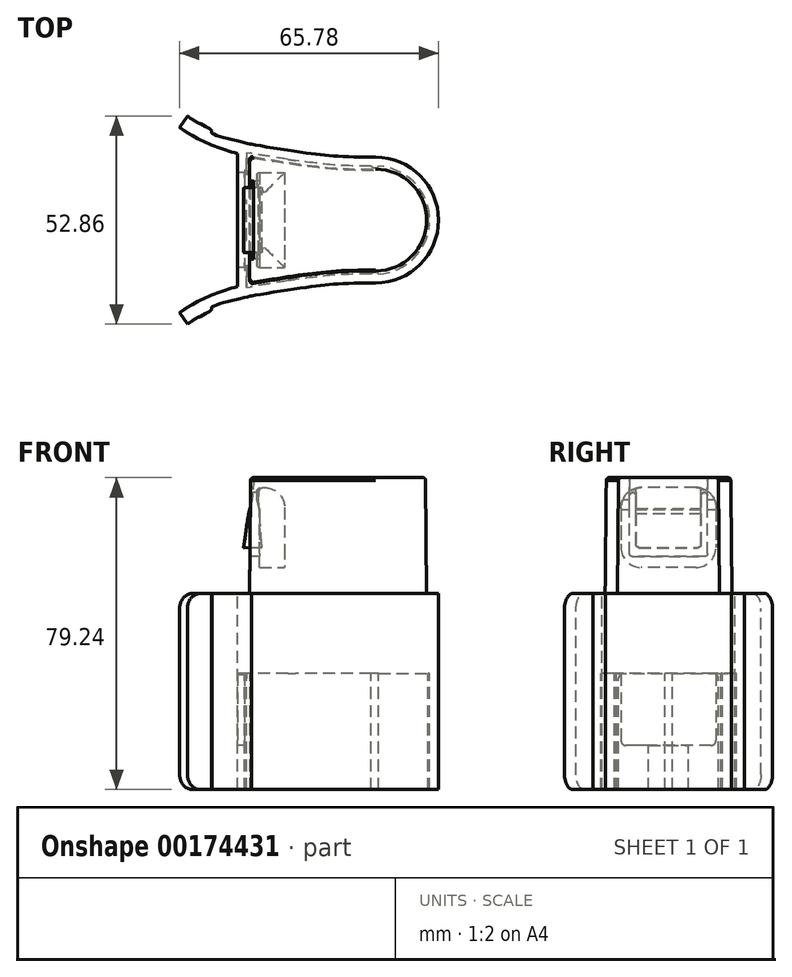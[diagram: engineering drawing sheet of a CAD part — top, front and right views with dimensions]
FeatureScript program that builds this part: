
annotation { "Feature Type Name" : "Feature", "Feature Type Description" : "" }
export const myFeature = defineFeature(function(context is Context, id is Id, definition is map)
    precondition{}
    {
        {
            var Q0;
            Q0=qCreatedBy(makeId("Top.planeOp"),FACE);
            var sketch = newSketch(context, id + "F0", { "sketchPlane" : qUnion([Q0])});
            skLineSegment(sketch, "E0", {"start": v(0, 0) * mm, "end": v(-39.58, 0) * mm, "construction": true});
            skArc(sketch, "E1", {"start": v(0, -12.95) * mm, "mid": v(12.95, 0) * mm, "end": v(0, 12.95) * mm});
            skLineSegment(sketch, "E2", {"start": v(-32, 16.26) * mm, "end": v(-32, -16.26) * mm});
            skPoint(sketch, "E3", {"position": v(-32, 0) * mm});
            skFitSpline(sketch, "E4", {"points": [v(0, 12.95) * mm, v(-14.22, 13.59) * mm, v(-32, 16.26) * mm], "startDerivative": vector(-40.46, 0) * mm, "endDerivative": vector(-35.46, 6.25) * mm});
            skLineSegment(sketch, "E5", {"start": v(-32, 16.26) * mm, "end": v(60.19, 0) * mm, "construction": true});
            skLineSegment(sketch, "E6", {"start": v(0, 12.95) * mm, "end": v(-13.28, 12.95) * mm, "construction": true});
            skFitSpline(sketch, "E7.MirrorCS", {"points": [v(0, -12.95) * mm, v(-14.22, -13.59) * mm, v(-32, -16.26) * mm], "startDerivative": vector(-40.46, 0) * mm, "endDerivative": vector(-35.46, -6.25) * mm});
            skSolve(sketch);
        }
        {
            var Q0;
            Q0=qCreatedBy(makeId("Top.planeOp"),FACE);
            var sketch = newSketch(context, id + "F1", { "sketchPlane" : qUnion([Q0])});
            skFitSpline(sketch, "E8.0", {"points": [v(0, 16) * mm, v(-1.67, 16) * mm, v(-4.6, 16.02) * mm, v(-7.54, 16.11) * mm, v(-9.71, 16.24) * mm, v(-11.32, 16.36) * mm, v(-12.96, 16.51) * mm, v(-14.7, 16.7) * mm, v(-16.57, 16.94) * mm, v(-19.19, 17.28) * mm, v(-22.67, 17.8) * mm, v(-27.05, 18.5) * mm, v(-30, 19) * mm, v(-31.47, 19.26) * mm]});
            skArc(sketch, "E8.1", {"start": v(0, -16) * mm, "mid": v(16, 0) * mm, "end": v(0, 16) * mm});
            skFitSpline(sketch, "E8.2", {"points": [v(0, -16) * mm, v(-1.67, -16) * mm, v(-4.6, -16.02) * mm, v(-7.54, -16.11) * mm, v(-9.71, -16.24) * mm, v(-11.32, -16.36) * mm, v(-12.96, -16.51) * mm, v(-14.7, -16.7) * mm, v(-16.57, -16.94) * mm, v(-19.19, -17.28) * mm, v(-22.67, -17.8) * mm, v(-27.05, -18.5) * mm, v(-30, -19) * mm, v(-31.47, -19.26) * mm]});
            skLineSegment(sketch, "E8.3", {"start": v(-35.05, 19.59) * mm, "end": v(-35.05, -19.59) * mm, "construction": true});
            skFitSpline(sketch, "E9", {"points": [v(-31.47, 19.26) * mm, v(-41.53, 22.07) * mm, v(-41.6, 22.64) * mm, v(-47.78, 26.43) * mm], "startDerivative": vector(1.67, -0.3) * mm, "endDerivative": vector(-19.6, 14.64) * mm});
            skArc(sketch, "E10", {"start": v(-49.78, 23.5) * mm, "mid": v(-41.28, 18.93) * mm, "end": v(-32, 16.26) * mm});
            skLineSegment(sketch, "E11", {"start": v(-47.78, 26.43) * mm, "end": v(-49.78, 23.5) * mm});
            skLineSegment(sketch, "E12", {"start": v(0, 0) * mm, "end": v(-91.75, 0) * mm, "construction": true});
            skLineSegment(sketch, "E13", {"start": v(-35.05, 16.9) * mm, "end": v(-35.05, -16.9) * mm});
            skPoint(sketch, "E14", {"position": v(-35.05, 0) * mm});
            skArc(sketch, "E15.MirrorCS", {"start": v(-49.78, -23.5) * mm, "mid": v(-41.28, -18.93) * mm, "end": v(-32, -16.26) * mm});
            skLineSegment(sketch, "E16.MirrorCS", {"start": v(-47.78, -26.43) * mm, "end": v(-49.78, -23.5) * mm});
            skFitSpline(sketch, "E17.MirrorCS", {"points": [v(-31.47, -19.26) * mm, v(-41.53, -22.07) * mm, v(-41.6, -22.64) * mm, v(-47.78, -26.43) * mm], "startDerivative": vector(1.67, 0.3) * mm, "endDerivative": vector(-19.6, -14.64) * mm});
            skSolve(sketch);
        }
        {
            var Q0;
            Q0=makeQuery(id+"F0.imprint","IMPRINT",FACE,{"disambiguationData":[TD([[makeQuery(id+"F0.imprint","IMPRINT",EDGE,{"derivedFrom":sQuery(id+"F0.wireOp",EDGE,"E1")}),1.0]])]});
            extrude(context, id + "F2", {"entities" : qUnion([Q0]), "depth" : 29.46 * mm, "hasDraft" : true, "draftAngle" : .5 * degree, "draftPullDirection" : true});
        }
        {
            var Q0;
            Q0 = qSketchRegion(id + "F1", true);
            extrude(context, id + "F3", {"entities" : qUnion([Q0]), "operationType" : NewBodyOperationType.ADD, "oppositeDirection" : true, "depth" : 49.78 * mm});
        }
        {
            var Q0;
            Q0=makeQuery(id+"F2.opExtrude","SWEPT_FACE",FACE,{"disambiguationData":[OSD([sQuery(id+"F0.wireOp",EDGE,"E2")])]});
            var sketch = newSketch(context, id + "F4", { "sketchPlane" : qUnion([Q0])});
            skLineSegment(sketch, "E18.bottom", {"start": v(-9.9, 25.38) * mm, "end": v(-8.26, 25.38) * mm});
            skLineSegment(sketch, "E18.top", {"start": v(-9.9, 9.12) * mm, "end": v(9.9, 9.12) * mm});
            skLineSegment(sketch, "E18.left", {"start": v(-9.9, 25.38) * mm, "end": v(-9.9, 9.12) * mm});
            skLineSegment(sketch, "E18.right", {"start": v(9.9, 25.38) * mm, "end": v(9.9, 9.12) * mm});
            skLineSegment(sketch, "E19.top", {"start": v(-8.26, 11.91) * mm, "end": v(8.26, 11.91) * mm});
            skLineSegment(sketch, "E19.left", {"start": v(-8.26, 25.38) * mm, "end": v(-8.26, 11.91) * mm});
            skLineSegment(sketch, "E19.right", {"start": v(8.26, 25.38) * mm, "end": v(8.26, 11.91) * mm});
            skLineSegment(sketch, "E20.trimOffspring", {"start": v(8.26, 25.38) * mm, "end": v(9.9, 25.38) * mm});
            skLineSegment(sketch, "E21", {"start": v(-8.26, 25.38) * mm, "end": v(8.26, 25.38) * mm, "construction": true});
            skPoint(sketch, "E22", {"position": v(0, 25.38) * mm});
            skPoint(sketch, "E23", {"position": v(0, 9.12) * mm});
            skSolve(sketch);
        }
        {
            var Q0;
            Q0=qCreatedBy(makeId("Top.planeOp"),FACE);
            cPlane(context, id + "F5", {"entities" : qUnion([Q0]), "cplaneType" : CPlaneType.OFFSET, "offset" : 20.32 * mm, "oppositeDirection" : true, "width" : 152.4 * mm, "height" : 152.4 * mm});
        }
        {
            var Q0;
            Q0=qCreatedBy(id+"F5.planeOp",FACE);
            var sketch = newSketch(context, id + "F6", { "sketchPlane" : qUnion([Q0])});
            skFitSpline(sketch, "E24.0", {"points": [v(0, 12.95) * mm, v(-6.35, 12.95) * mm, v(-13.52, 13.25) * mm, v(-25.75, 15.15) * mm, v(-32, 16.26) * mm], "construction": true});
            skArc(sketch, "E24.1", {"start": v(0, -12.95) * mm, "mid": v(12.95, 0) * mm, "end": v(0, 12.95) * mm, "construction": true});
            skFitSpline(sketch, "E24.2", {"points": [v(0, -12.95) * mm, v(-6.35, -12.95) * mm, v(-13.52, -13.25) * mm, v(-25.75, -15.15) * mm, v(-32, -16.26) * mm], "construction": true});
            skLineSegment(sketch, "E24.3", {"start": v(-32, 16.26) * mm, "end": v(-32, -16.26) * mm, "construction": true});
            skFitSpline(sketch, "E25.0", {"points": [v(0, 13.72) * mm, v(-1.68, 13.72) * mm, v(-4.63, 13.74) * mm, v(-7.63, 13.83) * mm, v(-9.86, 13.96) * mm, v(-11.51, 14.08) * mm, v(-13.19, 14.24) * mm, v(-14.96, 14.44) * mm, v(-16.86, 14.67) * mm, v(-19.5, 15.02) * mm, v(-23.02, 15.53) * mm, v(-27.42, 16.24) * mm, v(-30.4, 16.75) * mm, v(-31.87, 17) * mm]});
            skArc(sketch, "E25.1", {"start": v(0.77, -13.7) * mm, "mid": v(9.63, -9.76) * mm, "end": v(13.68, -0.95) * mm});
            skFitSpline(sketch, "E25.2", {"points": [v(0, -13.72) * mm, v(-1.68, -13.72) * mm, v(-4.63, -13.74) * mm, v(-7.63, -13.83) * mm, v(-9.86, -13.96) * mm, v(-11.51, -14.08) * mm, v(-13.19, -14.24) * mm, v(-14.96, -14.44) * mm, v(-16.86, -14.67) * mm, v(-19.5, -15.02) * mm, v(-23.02, -15.53) * mm, v(-27.42, -16.24) * mm, v(-30.4, -16.75) * mm, v(-31.87, -17) * mm]});
            skLineSegment(sketch, "E25.3", {"start": v(-32.77, 17.2) * mm, "end": v(-32.77, 12.7) * mm});
            skLineSegment(sketch, "E26", {"start": v(-31.87, 17) * mm, "end": v(-32.77, 17.2) * mm});
            skLineSegment(sketch, "E27", {"start": v(-31.87, -17) * mm, "end": v(-32.77, -17.17) * mm});
            skArc(sketch, "E28", {"start": v(13.68, 0.95) * mm, "mid": v(13.25, 0) * mm, "end": v(13.68, -0.95) * mm});
            skArc(sketch, "E29", {"start": v(-1.14, 13.72) * mm, "mid": v(-0.19, 13.28) * mm, "end": v(0.77, 13.7) * mm});
            skArc(sketch, "E30", {"start": v(-22.26, 15.43) * mm, "mid": v(-21.38, 14.86) * mm, "end": v(-20.38, 15.15) * mm});
            skArc(sketch, "E31", {"start": v(-20.38, -15.15) * mm, "mid": v(-21.38, -14.86) * mm, "end": v(-22.26, -15.43) * mm});
            skArc(sketch, "E32", {"start": v(0.77, -13.7) * mm, "mid": v(-0.19, -13.28) * mm, "end": v(-1.14, -13.72) * mm});
            skLineSegment(sketch, "E33.bottom", {"start": v(-32.77, -12.7) * mm, "end": v(-33.27, -12.7) * mm});
            skLineSegment(sketch, "E33.top", {"start": v(-32.77, -5.08) * mm, "end": v(-33.27, -5.08) * mm});
            skLineSegment(sketch, "E33.right", {"start": v(-33.27, -12.7) * mm, "end": v(-33.27, -5.08) * mm});
            skLineSegment(sketch, "E34.bottom", {"start": v(-32.77, 5.08) * mm, "end": v(-33.27, 5.08) * mm});
            skLineSegment(sketch, "E34.top", {"start": v(-32.77, 12.7) * mm, "end": v(-33.27, 12.7) * mm});
            skLineSegment(sketch, "E34.right", {"start": v(-33.27, 5.08) * mm, "end": v(-33.27, 12.7) * mm});
            skLineSegment(sketch, "E35", {"start": v(-33.27, -5.08) * mm, "end": v(-33.27, 5.08) * mm, "construction": true});
            skPoint(sketch, "E36", {"position": v(-33.27, 0) * mm});
            skLineSegment(sketch, "E37.trimOffspring", {"start": v(-32.77, -12.7) * mm, "end": v(-32.77, -17.17) * mm});
            skLineSegment(sketch, "E38.trimOffspring", {"start": v(-32.77, 5.08) * mm, "end": v(-32.77, -5.08) * mm});
            skFitSpline(sketch, "E39.trimOffspring", {"points": [v(0, -13.72) * mm, v(-1.68, -13.72) * mm, v(-4.63, -13.74) * mm, v(-7.63, -13.83) * mm, v(-9.86, -13.96) * mm, v(-11.51, -14.08) * mm, v(-13.19, -14.24) * mm, v(-14.96, -14.44) * mm, v(-16.86, -14.67) * mm, v(-19.5, -15.02) * mm, v(-23.02, -15.53) * mm, v(-27.42, -16.24) * mm, v(-30.4, -16.75) * mm, v(-31.87, -17) * mm]});
            skArc(sketch, "E40.trimOffspring", {"start": v(13.68, 0.95) * mm, "mid": v(9.63, 9.76) * mm, "end": v(0.77, 13.7) * mm});
            skFitSpline(sketch, "E41.trimOffspring", {"points": [v(0, 13.72) * mm, v(-1.68, 13.72) * mm, v(-4.63, 13.74) * mm, v(-7.63, 13.83) * mm, v(-9.86, 13.96) * mm, v(-11.51, 14.08) * mm, v(-13.19, 14.24) * mm, v(-14.96, 14.44) * mm, v(-16.86, 14.67) * mm, v(-19.5, 15.02) * mm, v(-23.02, 15.53) * mm, v(-27.42, 16.24) * mm, v(-30.4, 16.75) * mm, v(-31.87, 17) * mm]});
            skSolve(sketch);
        }
        {
            var Q0;
            Q0 = qSketchRegion(id + "F6", true);
            extrude(context, id + "F7", {"entities" : qUnion([Q0]), "operationType" : NewBodyOperationType.REMOVE, "endBound" : BoundingType.UP_TO_NEXT, "oppositeDirection" : true, "depth" : 25.4 * mm});
        }
        {
            var Q0;
            Q0=qCreatedBy(makeId("Front.planeOp"),FACE);
            var sketch = newSketch(context, id + "F8", { "sketchPlane" : qUnion([Q0])});
            skFitSpline(sketch, "E42.0.0", {"points": [v(-31.75, 29.46) * mm, v(-21.16, 29.46) * mm, v(-10.58, 29.46) * mm, v(0, 29.46) * mm], "construction": true});
            skLineSegment(sketch, "E42.0.1", {"start": v(0, 29.46) * mm, "end": v(12.7, 29.46) * mm, "construction": true});
            skFitSpline(sketch, "E42.0.2", {"points": [v(0, 29.46) * mm, v(-10.58, 29.46) * mm, v(-21.16, 29.46) * mm, v(-31.75, 29.46) * mm]});
            skFitSpline(sketch, "E43", {"points": [v(-31.06, 29.46) * mm, v(-31.3, 24.68) * mm, v(-32.59, 18.3) * mm, v(-33.38, 12.65) * mm, v(-33.5, 11.63) * mm], "startDerivative": vector(0.39, -18.89) * mm, "endDerivative": vector(0.18, -15.34) * mm});
            skLineSegment(sketch, "E44", {"start": v(-31.06, 29.46) * mm, "end": v(-33.94, 29.46) * mm});
            skLineSegment(sketch, "E45", {"start": v(-33.94, 29.46) * mm, "end": v(-33.5, 11.63) * mm});
            skLineSegment(sketch, "E46", {"start": v(-33.5, 11.63) * mm, "end": v(-28.87, 11.75) * mm});
            skLineSegment(sketch, "E47", {"start": v(-28.87, 11.75) * mm, "end": v(-29.77, 24.68) * mm});
            skArc(sketch, "E48", {"start": v(-27.53, 29.46) * mm, "mid": v(-29.27, 27.36) * mm, "end": v(-29.77, 24.68) * mm});
            skLineSegment(sketch, "E49", {"start": v(-31.06, 29.46) * mm, "end": v(-27.53, 29.46) * mm});
            skSolve(sketch);
        }
        {
            var Q0;
            {var subQ0=sQuery(id+"F8.wireOp",EDGE,"E43");Q0=makeQuery(id+"F8.imprint","IMPRINT",FACE,{"disambiguationData":[TD([[makeQuery(id+"F8.imprint","IMPRINT",EDGE,{"derivedFrom":subQ0}),-1.0]])]});}
            extrude(context, id + "F9", {"entities" : qUnion([Q0]), "operationType" : NewBodyOperationType.REMOVE, "endBound" : BoundingType.SYMMETRIC, "depth" : 19.8 * mm});
        }
        {
            var Q0;
            Q0=qCreatedBy(makeId("Front.planeOp"),FACE);
            var sketch = newSketch(context, id + "F10", { "sketchPlane" : qUnion([Q0])});
            skLineSegment(sketch, "E50.bottom", {"start": v(-29.46, 26.92) * mm, "end": v(-23.11, 26.92) * mm});
            skLineSegment(sketch, "E50.top", {"start": v(-29.46, 6.6) * mm, "end": v(-23.11, 6.6) * mm});
            skLineSegment(sketch, "E50.left", {"start": v(-29.46, 26.92) * mm, "end": v(-29.46, 6.6) * mm});
            skLineSegment(sketch, "E50.right", {"start": v(-23.11, 26.92) * mm, "end": v(-23.11, 6.6) * mm});
            skLineSegment(sketch, "E51", {"start": v(-29.46, 26.92) * mm, "end": v(-30.1, 26.28) * mm});
            skLineSegment(sketch, "E52", {"start": v(-30.1, 26.28) * mm, "end": v(-30.1, 23.83) * mm});
            skLineSegment(sketch, "E53", {"start": v(-30.1, 23.83) * mm, "end": v(-29.46, 21.25) * mm});
            skSolve(sketch);
        }
        {
            var Q0;
            Q0 = qSketchRegion(id + "F10", true);
            extrude(context, id + "F11", {"entities" : qUnion([Q0]), "operationType" : NewBodyOperationType.REMOVE, "endBound" : BoundingType.SYMMETRIC, "oppositeDirection" : true, "depth" : 24.13 * mm});
        }
        {
            var Q0;
            Q0 = qSketchRegion(id + "F4", true);
            extrude(context, id + "F12", {"entities" : qUnion([Q0]), "operationType" : NewBodyOperationType.REMOVE, "endBound" : BoundingType.UP_TO_NEXT, "oppositeDirection" : true, "depth" : 25.4 * mm});
        }
        {
            var Q0;
            Q0=makeQuery(id+"F8.imprint","IMPRINT",FACE,{"disambiguationData":[TD([[makeQuery(id+"F8.imprint","IMPRINT",EDGE,{"derivedFrom":sQuery(id+"F8.wireOp",EDGE,"E43")}),1.0]])]});
            extrude(context, id + "F13", {"entities" : qUnion([Q0]), "operationType" : NewBodyOperationType.ADD, "endBound" : BoundingType.SYMMETRIC, "depth" : 16.5 * mm});
        }
        {
            var Q0;
            Q0=makeQuery(id+"F13.opExtrude","CAP_EDGE",EDGE,{"disambiguationData":[OSD([sQuery(id+"F8.wireOp",EDGE,"E46")])],"isStart":true});
            var Q1;
            Q1=makeQuery(id+"F13.opExtrude","CAP_EDGE",EDGE,{"disambiguationData":[OSD([sQuery(id+"F8.wireOp",EDGE,"E46")])],"isStart":false});
            var Q2;
            Q2=makeQuery(id+"F12.boolean.opBoolean","COPY",EDGE,{"derivedFrom":makeQuery(id+"F12.opExtrude","SWEPT_EDGE",EDGE,{"disambiguationData":[OSD([sQuery(id+"F4.wireOp",EDGE,"E18.right"),sQuery(id+"F4.wireOp",EDGE,"E20.trimOffspring")])]})});
            var Q3;
            Q3=makeQuery(id+"F12.boolean.opBoolean","COPY",EDGE,{"derivedFrom":makeQuery(id+"F12.opExtrude","SWEPT_EDGE",EDGE,{"disambiguationData":[OSD([sQuery(id+"F4.wireOp",EDGE,"E19.right"),sQuery(id+"F4.wireOp",EDGE,"E20.trimOffspring")])]})});
            var Q4;
            Q4=makeQuery(id+"F12.boolean.opBoolean","COPY",EDGE,{"derivedFrom":makeQuery(id+"F12.opExtrude","SWEPT_EDGE",EDGE,{"disambiguationData":[OSD([sQuery(id+"F4.wireOp",EDGE,"E18.bottom"),sQuery(id+"F4.wireOp",EDGE,"E18.left")])]})});
            var Q5;
            Q5=makeQuery(id+"F12.boolean.opBoolean","COPY",EDGE,{"derivedFrom":makeQuery(id+"F12.opExtrude","SWEPT_EDGE",EDGE,{"disambiguationData":[OSD([sQuery(id+"F4.wireOp",EDGE,"E18.top"),sQuery(id+"F4.wireOp",EDGE,"E18.left")])]})});
            var Q6;
            Q6=makeQuery(id+"F12.boolean.opBoolean","COPY",EDGE,{"derivedFrom":makeQuery(id+"F12.opExtrude","SWEPT_EDGE",EDGE,{"disambiguationData":[OSD([sQuery(id+"F4.wireOp",EDGE,"E18.top"),sQuery(id+"F4.wireOp",EDGE,"E18.right")])]})});
            var Q7;
            Q7=makeQuery(id+"F2.opExtrude","CAP_EDGE",EDGE,{"disambiguationData":[OSD([sQuery(id+"F0.wireOp",EDGE,"E4")])],"isStart":false});
            var Q8;
            {var subQ0=sQuery(id+"F0.wireOp",EDGE,"E4");var subQ1=sQuery(id+"F0.wireOp",EDGE,"E2");Q8=makeQuery(id+"F9.boolean.opBoolean","SPLIT",EDGE,{"disambiguationData":[TD([makeQuery(id+"F2.opExtrude","SWEPT_FACE",FACE,{"disambiguationData":[OSD([subQ0])]})])],"derivedFrom":makeQuery(id+"F2.opExtrude","CAP_EDGE",EDGE,{"disambiguationData":[OSD([subQ1])],"isStart":false})});}
            var Q9;
            {var subQ0=sQuery(id+"F0.wireOp",EDGE,"E7.MirrorCS");var subQ1=sQuery(id+"F0.wireOp",EDGE,"E2");Q9=makeQuery(id+"F9.boolean.opBoolean","SPLIT",EDGE,{"disambiguationData":[TD([makeQuery(id+"F2.opExtrude","SWEPT_FACE",FACE,{"disambiguationData":[OSD([subQ0])]})])],"derivedFrom":makeQuery(id+"F2.opExtrude","CAP_EDGE",EDGE,{"disambiguationData":[OSD([subQ1])],"isStart":false})});}
            var Q10;
            Q10=makeQuery(id+"F2.opExtrude","SWEPT_EDGE",EDGE,{"disambiguationData":[OSD([sQuery(id+"F0.wireOp",EDGE,"E2"),sQuery(id+"F0.wireOp",EDGE,"E4")])]});
            var Q11;
            Q11=makeQuery(id+"F2.opExtrude","SWEPT_EDGE",EDGE,{"disambiguationData":[OSD([sQuery(id+"F0.wireOp",EDGE,"E2"),sQuery(id+"F0.wireOp",EDGE,"E7.MirrorCS")])]});
            var Q12;
            Q12=makeQuery(id+"F9.boolean.opBoolean","COPY",EDGE,{"derivedFrom":makeQuery(id+"F9.opExtrude","SWEPT_EDGE",EDGE,{"disambiguationData":[OSD([sQuery(id+"F8.wireOp",EDGE,"E43"),sQuery(id+"F8.wireOp",EDGE,"E44"),sQuery(id+"F8.wireOp",EDGE,"E49")])]})});
            var Q13;
            Q13=makeQuery(id+"F9.boolean.opBoolean","COPY",EDGE,{"derivedFrom":makeQuery(id+"F9.opExtrude","CAP_EDGE",EDGE,{"disambiguationData":[OSD([sQuery(id+"F8.wireOp",EDGE,"E44")])],"isStart":false})});
            var Q14;
            Q14=makeQuery(id+"F9.boolean.opBoolean","COPY",EDGE,{"derivedFrom":makeQuery(id+"F9.opExtrude","CAP_EDGE",EDGE,{"disambiguationData":[OSD([sQuery(id+"F8.wireOp",EDGE,"E44")])],"isStart":true})});
            var Q15;
            Q15=makeQuery(id+"F12.boolean.opBoolean","COPY",EDGE,{"derivedFrom":makeQuery(id+"F12.opExtrude","SWEPT_EDGE",EDGE,{"disambiguationData":[OSD([sQuery(id+"F4.wireOp",EDGE,"E18.bottom"),sQuery(id+"F4.wireOp",EDGE,"E19.left")])]})});
            fillet(context, id + "F14", {"entities" : qUnion([Q0, Q1, Q2, Q3, Q4, Q5, Q6, Q7, Q8, Q9, Q10, Q11, Q12, Q13, Q14, Q15]), "radius" : 0.76 * mm, "tangentPropagation" : true, "allowEdgeOverflow" : false});
        }
        {
            var Q0;
            Q0=makeQuery(id+"F3.opExtrude","SWEPT_FACE",FACE,{"disambiguationData":[OSD([sQuery(id+"F1.wireOp",EDGE,"E13")])]});
            var sketch = newSketch(context, id + "F15", { "sketchPlane" : qUnion([Q0])});
            skLineSegment(sketch, "E54.bottom", {"start": v(-12.06, -20.32) * mm, "end": v(12.06, -20.32) * mm});
            skLineSegment(sketch, "E54.top", {"start": v(-12.06, -38.6) * mm, "end": v(12.07, -38.6) * mm});
            skLineSegment(sketch, "E54.left", {"start": v(-12.06, -20.32) * mm, "end": v(-12.06, -38.6) * mm});
            skLineSegment(sketch, "E54.right", {"start": v(12.07, -20.32) * mm, "end": v(12.07, -38.6) * mm});
            skPoint(sketch, "E55", {"position": v(0, -20.32) * mm});
            skSolve(sketch);
        }
        {
            var Q0;
            Q0 = qSketchRegion(id + "F15", true);
            extrude(context, id + "F16", {"entities" : qUnion([Q0]), "operationType" : NewBodyOperationType.REMOVE, "endBound" : BoundingType.UP_TO_NEXT, "oppositeDirection" : true, "depth" : 25.4 * mm});
        }
        {
            var Q0;
            {var subQ0=sQuery(id+"F6.wireOp",EDGE,"E34.top");Q0=makeQuery(id+"F16.boolean.opBoolean","MERGE",EDGE,{"derivedFrom":[makeQuery(id+"F7.boolean.opBoolean","COPY",EDGE,{"derivedFrom":makeQuery(id+"F7.opExtrude","CAP_EDGE",EDGE,{"disambiguationData":[OSD([subQ0])],"isStart":true})}),makeQuery(id+"F16.opExtrude","SWEPT_EDGE",EDGE,{"disambiguationData":[OSD([subQ0,sQuery(id+"F6.wireOp",EDGE,"E34.right")])]})]});}
            var Q1;
            Q1=makeQuery(id+"F16.boolean.opBoolean","COPY",EDGE,{"derivedFrom":makeQuery(id+"F16.opExtrude","SWEPT_EDGE",EDGE,{"disambiguationData":[OSD([sQuery(id+"F15.wireOp",EDGE,"E54.top"),sQuery(id+"F15.wireOp",EDGE,"E54.left")])]})});
            var Q2;
            Q2=makeQuery(id+"F16.boolean.opBoolean","COPY",EDGE,{"derivedFrom":makeQuery(id+"F16.opExtrude","SWEPT_EDGE",EDGE,{"disambiguationData":[OSD([sQuery(id+"F15.wireOp",EDGE,"E54.top"),sQuery(id+"F15.wireOp",EDGE,"E54.right")])]})});
            var Q3;
            {var subQ0=sQuery(id+"F6.wireOp",EDGE,"E33.bottom");Q3=makeQuery(id+"F16.boolean.opBoolean","MERGE",EDGE,{"derivedFrom":[makeQuery(id+"F7.boolean.opBoolean","COPY",EDGE,{"derivedFrom":makeQuery(id+"F7.opExtrude","CAP_EDGE",EDGE,{"disambiguationData":[OSD([subQ0])],"isStart":true})}),makeQuery(id+"F16.opExtrude","SWEPT_EDGE",EDGE,{"disambiguationData":[OSD([subQ0,sQuery(id+"F6.wireOp",EDGE,"E33.right")])]})]});}
            fillet(context, id + "F17", {"entities" : qUnion([Q0, Q1, Q2, Q3]), "radius" : 1.27 * mm, "tangentPropagation" : true, "allowEdgeOverflow" : false});
        }
        {
            var Q0;
            Q0=makeQuery(id+"F3.opExtrude","CAP_EDGE",EDGE,{"disambiguationData":[OSD([sQuery(id+"F1.wireOp",EDGE,"E16.MirrorCS")])],"isStart":false});
            var Q1;
            Q1=makeQuery(id+"F3.opExtrude","CAP_EDGE",EDGE,{"disambiguationData":[OSD([sQuery(id+"F1.wireOp",EDGE,"E11")])],"isStart":false});
            var Q2;
            Q2=makeQuery(id+"F3.opExtrude","CAP_EDGE",EDGE,{"disambiguationData":[OSD([sQuery(id+"F1.wireOp",EDGE,"E16.MirrorCS")])],"isStart":true});
            var Q3;
            Q3=makeQuery(id+"F3.opExtrude","CAP_EDGE",EDGE,{"disambiguationData":[OSD([sQuery(id+"F1.wireOp",EDGE,"E11")])],"isStart":true});
            fillet(context, id + "F18", {"entities" : qUnion([Q0, Q1, Q2, Q3]), "radius" : 3.8 * mm, "tangentPropagation" : true, "allowEdgeOverflow" : false});
        }
        {
            var Q0;
            Q0=makeQuery(id+"F13.boolean.opBoolean","INTERSECT",EDGE,{"derivedFrom":[makeQuery(id+"F11.boolean.opBoolean","COPY",FACE,{"derivedFrom":makeQuery(id+"F11.opExtrude","SWEPT_FACE",FACE,{"disambiguationData":[OSD([sQuery(id+"F10.wireOp",EDGE,"E50.bottom")])]})}),makeQuery(id+"F13.opExtrude","SWEPT_FACE",FACE,{"disambiguationData":[OSD([sQuery(id+"F8.wireOp",EDGE,"E48")])]})]});
            fillet(context, id + "F19", {"entities" : qUnion([Q0]), "radius" : 1.27 * mm, "tangentPropagation" : true, "allowEdgeOverflow" : false});
        }
        {
            var Q0;
            Q0=makeQuery(id+"F11.boolean.opBoolean","COPY",EDGE,{"derivedFrom":makeQuery(id+"F11.opExtrude","CAP_EDGE",EDGE,{"disambiguationData":[OSD([sQuery(id+"F10.wireOp",EDGE,"E50.bottom")])],"isStart":true})});
            var Q1;
            Q1=makeQuery(id+"F11.boolean.opBoolean","COPY",EDGE,{"derivedFrom":makeQuery(id+"F11.opExtrude","CAP_EDGE",EDGE,{"disambiguationData":[OSD([sQuery(id+"F10.wireOp",EDGE,"E50.bottom")])],"isStart":false})});
            var Q2;
            Q2=makeQuery(id+"F11.boolean.opBoolean","COPY",EDGE,{"derivedFrom":makeQuery(id+"F11.opExtrude","CAP_EDGE",EDGE,{"disambiguationData":[OSD([sQuery(id+"F10.wireOp",EDGE,"E50.top")])],"isStart":false})});
            var Q3;
            Q3=makeQuery(id+"F11.boolean.opBoolean","COPY",EDGE,{"derivedFrom":makeQuery(id+"F11.opExtrude","CAP_EDGE",EDGE,{"disambiguationData":[OSD([sQuery(id+"F10.wireOp",EDGE,"E50.top")])],"isStart":true})});
            var Q4;
            Q4=makeQuery(id+"F11.boolean.opBoolean","COPY",EDGE,{"derivedFrom":makeQuery(id+"F11.opExtrude","SWEPT_EDGE",EDGE,{"disambiguationData":[OSD([sQuery(id+"F10.wireOp",EDGE,"E50.bottom"),sQuery(id+"F10.wireOp",EDGE,"E50.right")])]})});
            fillet(context, id + "F20", {"entities" : qUnion([Q0, Q1, Q2, Q3, Q4]), "radius" : 5.08 * mm, "tangentPropagation" : true, "allowEdgeOverflow" : false});
        }
    });
